# Revit family: 95800037
name_source: partatom
category: Modelos genéricos
revit_build: Autodesk Revit 2016 (Build: 20150220_1215(x64)
units: mm (PartAtom-declared; Revit-internal decimal feet)

## family parameters
Com base no plano de trabalho = Não
Compartilhado = Não
Corte com vazios quando carregados = Não
Cota do conector redondo = Utilizar diâmetro
Pode hospedar o vergalhão = Não
Ponto de cálculo do ambiente = Não
Sempre na vertical = Sim
Tipo de parte = Normal

## types (1)
- Square Island Isla 40 Silent Black Steel
    Acabamento = Scotch brite
    Código de montagem = Square Island Isla 40 Silent Black Steel 95800037
    Descrição = Square Island Isla 40 Silent Black Steel 95800037
    Desenvolvedor = Factory Cursos & Desenvolvimento
    Espessura = 0,4 mm
    Fabricante = Tramontina
    Material = Black
    Potencia Eletrica Total = 220V
    Referencia = Square Island Isla 40 Silent Black Steel
    Ruido = 63 db
    Site do desenvolvedor = www.factorycursos.com.br
    Tensão / Frequencia = 220V / 50 - 60 Hz
    Tipo de imagem = <Nenhum>
    Tratamento anti digitais = Não
    URL = www.tramontina.com.br
    Vazão = 650 m3/h
